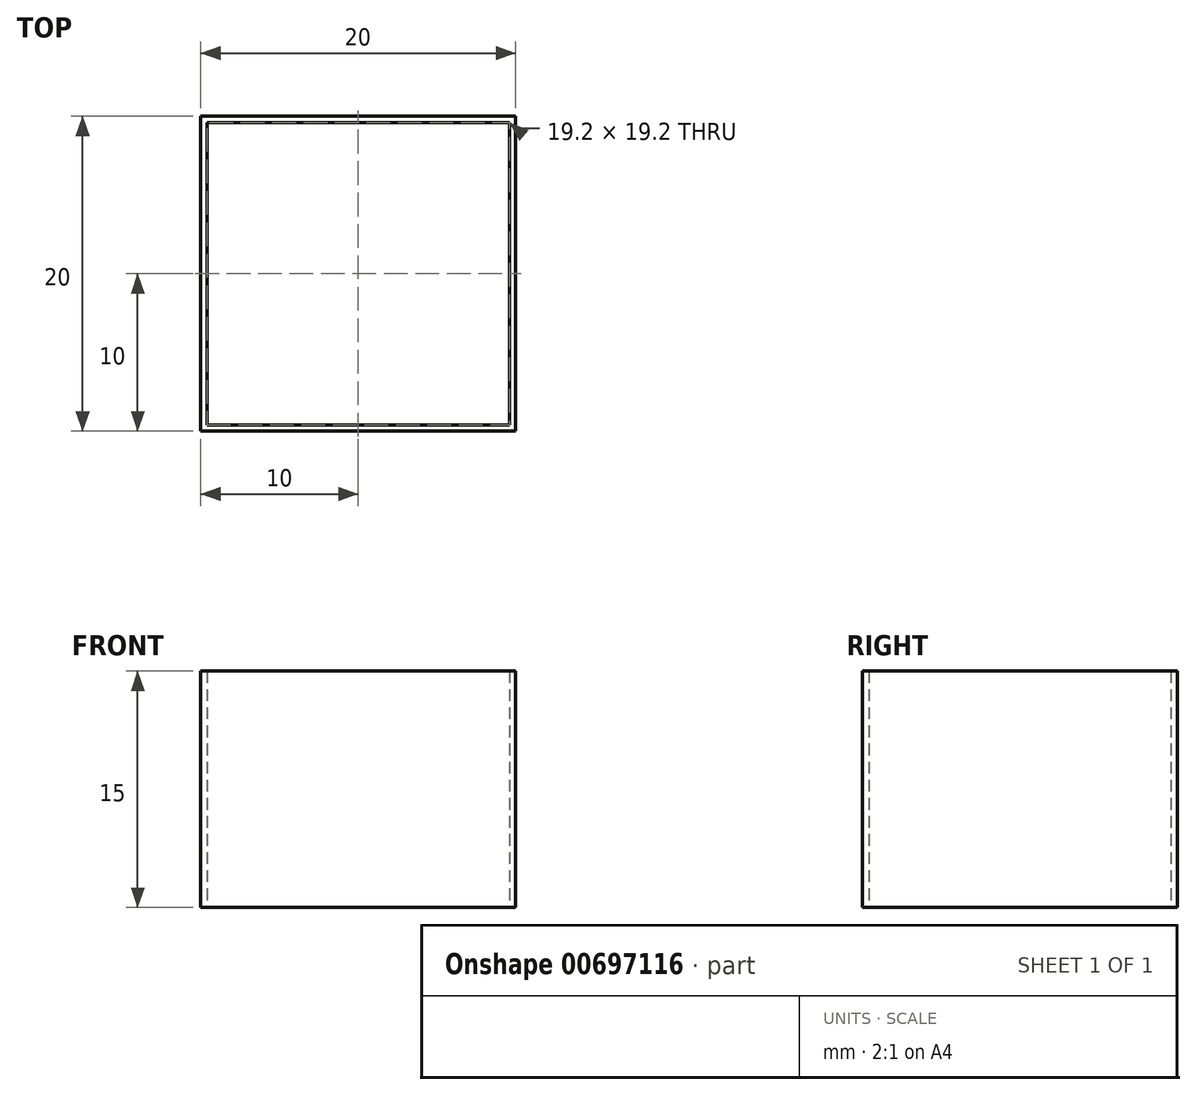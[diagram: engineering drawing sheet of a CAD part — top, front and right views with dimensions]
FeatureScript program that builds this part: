
annotation { "Feature Type Name" : "Feature", "Feature Type Description" : "" }
export const myFeature = defineFeature(function(context is Context, id is Id, definition is map)
    precondition{}
    {
        {
            var Q0;
            Q0=qCreatedBy(makeId("Top.planeOp"),FACE);
            var sketch = newSketch(context, id + "F0", { "sketchPlane" : qUnion([Q0])});
            skLineSegment(sketch, "E0.bottom", {"start": v(10, 10) * mm, "end": v(-10, 10) * mm});
            skLineSegment(sketch, "E0.top", {"start": v(10, -10) * mm, "end": v(-10, -10) * mm});
            skLineSegment(sketch, "E0.left", {"start": v(10, 10) * mm, "end": v(10, -10) * mm});
            skLineSegment(sketch, "E0.right", {"start": v(-10, 10) * mm, "end": v(-10, -10) * mm});
            skPoint(sketch, "E0.middle", {"position": v(0, 0) * mm});
            skSolve(sketch);
        }
        {
            var Q0;
            Q0 = qSketchRegion(id + "F0", true);
            extrude(context, id + "F1", {"entities" : qUnion([Q0]), "depth" : 15 * mm, "offsetDistance" : 25 * mm});
        }
        {
            var Q0;
            Q0=makeQuery(id+"F1.opExtrude","CAP_FACE",FACE,{"disambiguationData":[OSD([sQuery(id+"F0.wireOp",EDGE,"E0.bottom"),sQuery(id+"F0.wireOp",EDGE,"E0.top"),sQuery(id+"F0.wireOp",EDGE,"E0.left"),sQuery(id+"F0.wireOp",EDGE,"E0.right")])],"isStart":false});
            var Q1;
            Q1=makeQuery(id+"F1.opExtrude","CAP_FACE",FACE,{"disambiguationData":[OSD([sQuery(id+"F0.wireOp",EDGE,"E0.bottom"),sQuery(id+"F0.wireOp",EDGE,"E0.top"),sQuery(id+"F0.wireOp",EDGE,"E0.left"),sQuery(id+"F0.wireOp",EDGE,"E0.right")])],"isStart":true});
            var Q2;
            Q2=makeQuery(id+"F1.opExtrude","SWEPT_BODY",BODY,{"disambiguationData":[OSD([sQuery(id+"F0.wireOp",EDGE,"E0.bottom"),sQuery(id+"F0.wireOp",EDGE,"E0.top"),sQuery(id+"F0.wireOp",EDGE,"E0.left"),sQuery(id+"F0.wireOp",EDGE,"E0.right")])]});
            shell(context, id + "F2", {"entities" : qUnion([Q0, Q1]), "parts" : qUnion([Q2]), "thickness" : 0.4 * mm});
        }
    });
